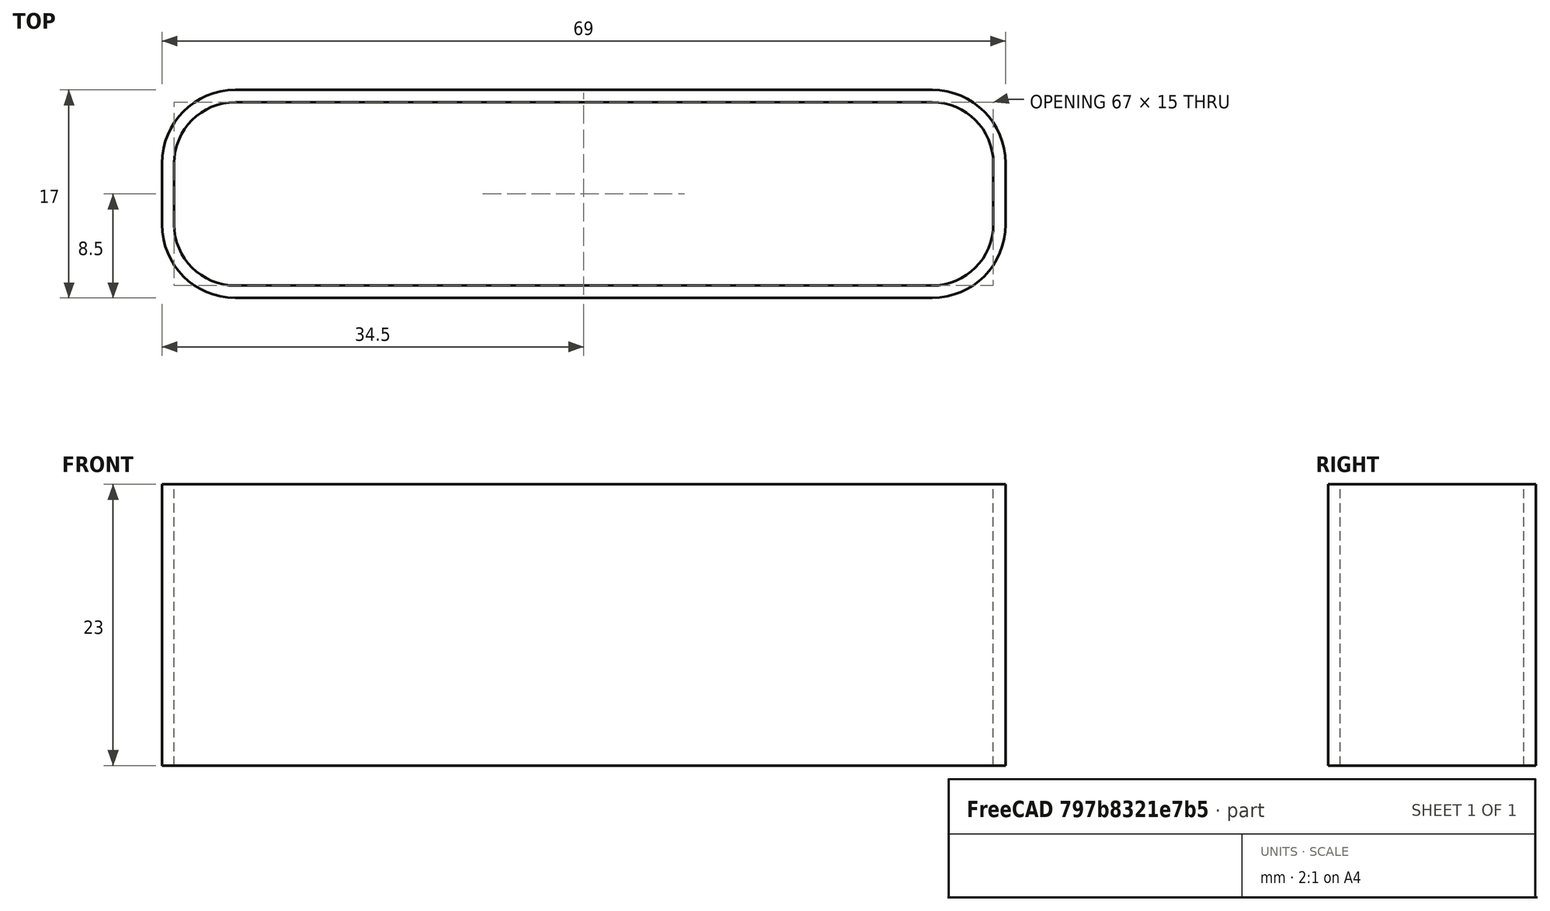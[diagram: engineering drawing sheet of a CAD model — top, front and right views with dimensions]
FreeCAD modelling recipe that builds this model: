
FCSTD DOCUMENT  (FreeCAD 0.20R29410 (Git))
Label: strap
License: All rights reserved
LicenseURL: http://en.wikipedia.org/wiki/All_rights_reserved
objects: Sketcher::SketchObject×1, PartDesign::Pad×1, PartDesign::Body×1
note: 4 computed .brp shape members not serialized (recipe doc carries the construction recipe); baked Part::Feature solids carry a one-line shape summary decoded from their .brp

FEATURE [Sketcher::SketchObject] Sketch
  FullyConstrained = true
  MapMode = 5
  Support = -> [XY_Plane]
  sketch-geometry (20):
    g0: ArcOfCircle CenterX=-63 CenterY=11 CenterZ=0 NormalX=0 NormalY=0 NormalZ=1 AngleXU=0 Radius=5 StartAngle=1.5708 EndAngle=3.14159
    g1: LineSegment StartX=-63 StartY=16 StartZ=0 EndX=-6 EndY=16 EndZ=0
    g2: ArcOfCircle CenterX=-6 CenterY=11 CenterZ=0 NormalX=0 NormalY=0 NormalZ=1 AngleXU=0 Radius=5 StartAngle=1e-16 EndAngle=1.5708
    g3: LineSegment StartX=-1 StartY=11 StartZ=0 EndX=-1 EndY=6 EndZ=0
    g4: ArcOfCircle CenterX=-6 CenterY=6 CenterZ=0 NormalX=0 NormalY=0 NormalZ=1 AngleXU=0 Radius=5 StartAngle=4.71239 EndAngle=6.28319
    g5: LineSegment StartX=-6 StartY=1 StartZ=0 EndX=-63 EndY=1 EndZ=0
    g6: ArcOfCircle CenterX=-63 CenterY=6 CenterZ=0 NormalX=0 NormalY=0 NormalZ=1 AngleXU=0 Radius=5 StartAngle=3.14159 EndAngle=4.71239
    g7: LineSegment StartX=-68 StartY=6 StartZ=0 EndX=-68 EndY=11 EndZ=0
    g8: GeomPoint X=-68 Y=16 Z=0
    g9: GeomPoint X=-1 Y=1 Z=0
    g10: ArcOfCircle CenterX=-63 CenterY=11 CenterZ=0 NormalX=0 NormalY=0 NormalZ=1 AngleXU=0 Radius=6 StartAngle=1.5708 EndAngle=3.14159
    g11: LineSegment StartX=-63 StartY=17 StartZ=0 EndX=-6 EndY=17 EndZ=0
    g12: ArcOfCircle CenterX=-6 CenterY=11 CenterZ=0 NormalX=0 NormalY=0 NormalZ=1 AngleXU=0 Radius=6 StartAngle=2e-16 EndAngle=1.5708
    g13: LineSegment StartX=0 StartY=11 StartZ=0 EndX=0 EndY=6 EndZ=0
    g14: ArcOfCircle CenterX=-6 CenterY=6 CenterZ=0 NormalX=0 NormalY=0 NormalZ=1 AngleXU=0 Radius=6 StartAngle=4.71239 EndAngle=6.28319
    g15: LineSegment StartX=-6 StartY=0 StartZ=0 EndX=-63 EndY=0 EndZ=0
    g16: ArcOfCircle CenterX=-63 CenterY=6 CenterZ=0 NormalX=0 NormalY=0 NormalZ=1 AngleXU=0 Radius=6 StartAngle=3.14159 EndAngle=4.71239
    g17: LineSegment StartX=-69 StartY=6 StartZ=0 EndX=-69 EndY=11 EndZ=0
    g18: GeomPoint X=-69 Y=17 Z=0
    g19: GeomPoint X=0 Y=0 Z=0
  constraints (47):
    c: Tangent(g0,g1) = 1.5708
    c: Tangent(g1,g2) = 1.5708
    c: Tangent(g2,g3) = 1.5708
    c: Tangent(g3,g4) = 1.5708
    c: Tangent(g4,g5) = 1.5708
    c: Tangent(g5,g6) = 1.5708
    c: Tangent(g6,g7) = 1.5708
    c: Tangent(g7,g0) = 1.5708
    c: Horizontal(g1)
    c: Horizontal(g5)
    c: Vertical(g3)
    c: Vertical(g7)
    c: Equal(g0,g2)
    c: Equal(g2,g4)
    c: Equal(g4,g6)
    c: PointOnObject(g8,g1)
    c: PointOnObject(g8,g7)
    c: PointOnObject(g9,g3)
    c: PointOnObject(g9,g5)
    c: DistanceX(g1,g1) = 57
    c: DistanceY(g2,g1) = 5
    c: Tangent(g10,g11) = 1.5708
    c: Tangent(g11,g12) = 1.5708
    c: Tangent(g12,g13) = 1.5708
    c: Tangent(g13,g14) = 1.5708
    c: Tangent(g14,g15) = 1.5708
    c: Tangent(g15,g16) = 1.5708
    c: Tangent(g16,g17) = 1.5708
    c: Tangent(g17,g10) = 1.5708
    c: Horizontal(g11)
    c: Horizontal(g15)
    c: Vertical(g13)
    c: Vertical(g17)
    c: Equal(g10,g12)
    c: Equal(g12,g14)
    c: Equal(g14,g16)
    c: PointOnObject(g18,g11)
    c: PointOnObject(g18,g17)
    c: PointOnObject(g19,g13)
    c: PointOnObject(g19,g15)
    c: DistanceY(g0,g10) = 1
    c: DistanceX(g10,g0) = 1
    c: DistanceX(g3,g13) = 1
    c: DistanceY(g14,g4) = 1
    c: DistanceX(g11,g11) = 57
    c: Coincident(g19,g-1)
    c: DistanceY(g5,g0) = 15
FEATURE [PartDesign::Pad] Pad
  Direction = (0,0,1)
  Length = 23
  Length2 = 10
  Profile = -> Sketch
  ReferenceAxis = -> Sketch [N_Axis]
  Type = 0
FEATURE [PartDesign::Body] Body
  Group = -> [Sketch,Pad]
  Origin = -> Origin
  Tip = -> Pad
